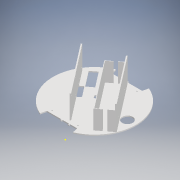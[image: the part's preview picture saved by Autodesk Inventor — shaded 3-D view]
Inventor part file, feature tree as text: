
AUTODESK INVENTOR PART (.ipt)
format: ipt  version: 2020 (Build 240168000, 168)  size: 323,072 bytes
history: native  units: mm
features: sketch x10, extrude x9, reference x9, other x3, projected_geometry x1
ambient origin geometry x8: Origin, YZ Plane, XZ Plane, XY Plane, X Axis, Y Axis, Z Axis, Center Point
bodies: Solid1 (feature_tree)
feature tree (32):
  extrude  "DnoKonstrukcije"  Depth=34.0mm TaperAngle=0.0deg
  extrude  "DrzacZaBateriju"  Depth=42.0mm TaperAngle=0.0deg
  extrude  "DrzacZaTeensy"  Depth=30.0mm
  extrude  "DrzacZaPDB"  Depth=35.0mm
  sketch  "Sketch10"  dims[d19=2.0mm d20=2.0mm]
  extrude  "RupeZaPDBSEkranom"  Depth=2.0mm
  extrude  "RupeZaDriverMotora"  Depth=2.0mm
  extrude  "RupeZaPDB"  Depth=30.0mm
  extrude  "RupeZaTeensy"  Depth=35.0mm
  extrude  "RupaZaLezaj"  Depth=2.0mm
  sketch  "Sketch1"  dims[d0=2.0mm d1=0.0mm d8=34.0mm d9=0.0mm]
  reference  "Reference7"
  sketch  "Sketch6"  dims[d10=10.0mm d11=0.0mm d12=42.0mm d13=0.0mm]
  reference  "Reference10"
  reference  "Reference11"
  reference  "Reference12"
  reference  "Reference13"
  sketch  "Sketch7"  dims[d14=2.0mm d15=0.0mm d16=30.0mm]
  projected_geometry  "Projected Loop2"
  sketch  "Sketch8"  dims[d17=35.0mm d18=2.5mm]
  reference  "Reference14"
  sketch  "Sketch11"  dims[d21=2.0mm d22=2.0mm]
  reference  "Reference17"
  reference  "Reference18"
  reference  "Reference19"
  sketch  "Sketch12"  dims[d23=2.0mm d24=0.0mm d25=30.0mm]
  sketch  "Sketch15"  dims[d26=35.0mm d27=2.5mm]
  sketch  "Sketch16"  dims[d28=2.0mm d29=2.0mm]
  sketch  "Sketch17"  dims[d30=2.0mm d31=2.0mm d32=2.0mm d33=0.0mm d34=65.0mm d35=35.0mm d36=2.5mm d37=2.0mm d38=2.0mm d39=2.0mm d40=2.0mm d41=2.0mm d42=0.0mm d43=58.784mm d44=19.0mm d45=2.0mm d46=0.0mm]
  other  "DonjaKons_V.5 - Copy.iam"
  other  "KonstrukcijaDonjiDio_v.3.:1"
  other  "mrm-ps3xc:1"
